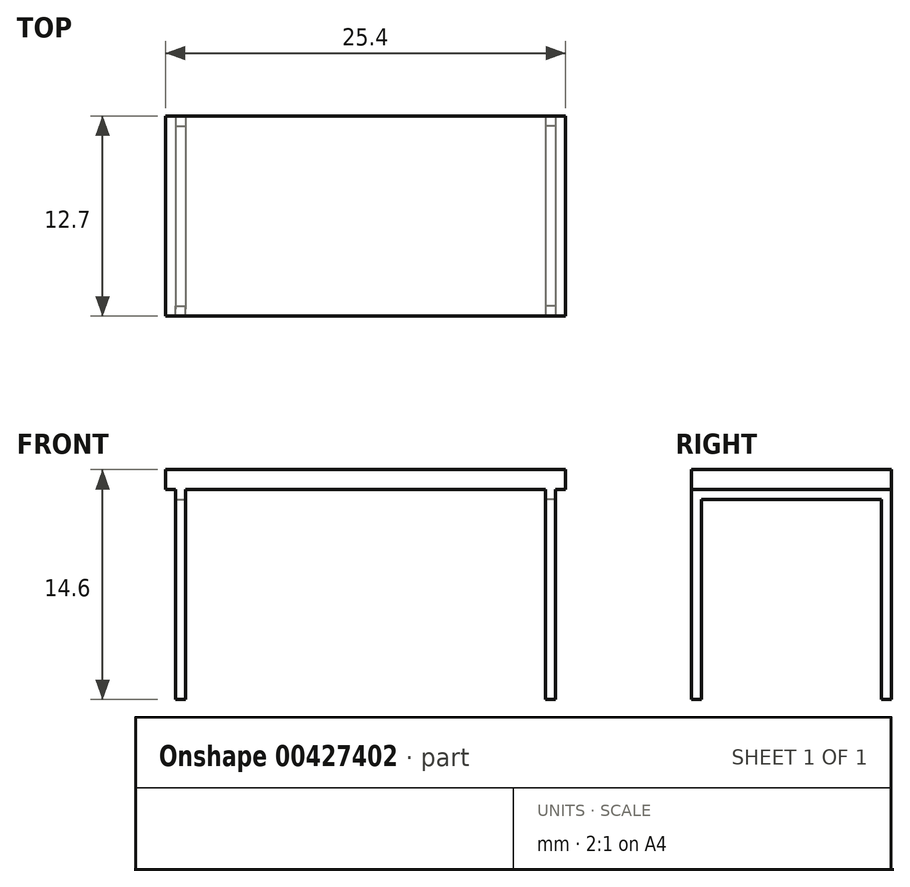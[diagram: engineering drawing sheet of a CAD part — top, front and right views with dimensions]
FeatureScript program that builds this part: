
annotation { "Feature Type Name" : "Feature", "Feature Type Description" : "" }
export const myFeature = defineFeature(function(context is Context, id is Id, definition is map)
    precondition{}
    {
        {
            var Q0;
            Q0=qCreatedBy(makeId("Top.planeOp"),FACE);
            var sketch = newSketch(context, id + "F0", { "sketchPlane" : qUnion([Q0])});
            skLineSegment(sketch, "E0.bottom", {"start": v(12.7, -6.35) * mm, "end": v(-12.7, -6.35) * mm});
            skLineSegment(sketch, "E0.top", {"start": v(12.7, 6.35) * mm, "end": v(-12.7, 6.35) * mm});
            skLineSegment(sketch, "E0.left", {"start": v(12.7, -6.35) * mm, "end": v(12.7, 6.35) * mm});
            skLineSegment(sketch, "E0.right", {"start": v(-12.7, -6.35) * mm, "end": v(-12.7, 6.35) * mm});
            skPoint(sketch, "E0.middle", {"position": v(0, 0) * mm});
            skSolve(sketch);
        }
        {
            var Q0;
            Q0 = qSketchRegion(id + "F0", true);
            extrude(context, id + "F1", {"entities" : qUnion([Q0]), "depth" : 1.27 * mm});
        }
        {
            var Q0;
            Q0=makeQuery(id+"F1.opExtrude","SWEPT_FACE",FACE,{"disambiguationData":[OSD([sQuery(id+"F0.wireOp",EDGE,"E0.bottom")])]});
            var sketch = newSketch(context, id + "F2", { "sketchPlane" : qUnion([Q0])});
            skLineSegment(sketch, "E1.right", {"start": v(-12.07, 0) * mm, "end": v(-12.07, -0.64) * mm});
            skLineSegment(sketch, "E2.bottom", {"start": v(-12.07, 0) * mm, "end": v(-11.43, 0) * mm});
            skLineSegment(sketch, "E2.top", {"start": v(-12.07, -0.64) * mm, "end": v(-11.43, -0.64) * mm});
            skLineSegment(sketch, "E2.right", {"start": v(-11.43, 0) * mm, "end": v(-11.43, -0.64) * mm});
            skLineSegment(sketch, "E3.MirrorCS", {"start": v(12.06, 0) * mm, "end": v(11.43, 0) * mm});
            skLineSegment(sketch, "E4.MirrorCS", {"start": v(11.43, 0) * mm, "end": v(11.43, -0.64) * mm});
            skLineSegment(sketch, "E5.MirrorCS", {"start": v(12.06, -0.64) * mm, "end": v(11.43, -0.64) * mm});
            skLineSegment(sketch, "E6.MirrorCS", {"start": v(12.06, 0) * mm, "end": v(12.06, -0.64) * mm});
            skSolve(sketch);
        }
        {
            var Q0;
            Q0 = qSketchRegion(id + "F2", true);
            extrude(context, id + "F3", {"entities" : qUnion([Q0]), "operationType" : NewBodyOperationType.ADD, "depth" : -12.7 * mm});
        }
        {
            var Q0;
            Q0=makeQuery(id+"F3.opExtrude","SWEPT_FACE",FACE,{"disambiguationData":[OSD([sQuery(id+"F2.wireOp",EDGE,"E5.MirrorCS")])]});
            var sketch = newSketch(context, id + "F4", { "sketchPlane" : qUnion([Q0])});
            skLineSegment(sketch, "E7.bottom", {"start": v(12.06, -6.35) * mm, "end": v(11.43, -6.35) * mm});
            skLineSegment(sketch, "E7.top", {"start": v(12.06, -5.72) * mm, "end": v(11.43, -5.72) * mm});
            skLineSegment(sketch, "E7.left", {"start": v(12.06, -6.35) * mm, "end": v(12.06, -5.72) * mm});
            skLineSegment(sketch, "E7.right", {"start": v(11.43, -6.35) * mm, "end": v(11.43, -5.72) * mm});
            skLineSegment(sketch, "E8.MirrorCS", {"start": v(12.06, 6.35) * mm, "end": v(11.43, 6.35) * mm});
            skLineSegment(sketch, "E9.MirrorCS", {"start": v(12.06, 6.35) * mm, "end": v(12.06, 5.72) * mm});
            skLineSegment(sketch, "E10.MirrorCS", {"start": v(11.43, 6.35) * mm, "end": v(11.43, 5.72) * mm});
            skLineSegment(sketch, "E11.MirrorCS", {"start": v(12.06, 5.72) * mm, "end": v(11.43, 5.72) * mm});
            skLineSegment(sketch, "E12.MirrorCS", {"start": v(-12.06, -6.35) * mm, "end": v(-12.06, -5.72) * mm});
            skLineSegment(sketch, "E13.MirrorCS", {"start": v(-12.06, -5.72) * mm, "end": v(-11.43, -5.72) * mm});
            skLineSegment(sketch, "E14.MirrorCS", {"start": v(-11.43, -6.35) * mm, "end": v(-11.43, -5.72) * mm});
            skLineSegment(sketch, "E15.MirrorCS", {"start": v(-12.06, -6.35) * mm, "end": v(-11.43, -6.35) * mm});
            skLineSegment(sketch, "E16.MirrorCS", {"start": v(-12.06, 6.35) * mm, "end": v(-12.06, 5.72) * mm});
            skLineSegment(sketch, "E17.MirrorCS", {"start": v(-11.43, 6.35) * mm, "end": v(-11.43, 5.72) * mm});
            skLineSegment(sketch, "E18.MirrorCS", {"start": v(-12.06, 5.72) * mm, "end": v(-11.43, 5.72) * mm});
            skLineSegment(sketch, "E19.MirrorCS", {"start": v(-12.06, 6.35) * mm, "end": v(-11.43, 6.35) * mm});
            skSolve(sketch);
        }
        {
            var Q0;
            Q0 = qSketchRegion(id + "F4", true);
            extrude(context, id + "F5", {"entities" : qUnion([Q0]), "operationType" : NewBodyOperationType.ADD, "depth" : 12.7 * mm});
        }
    });
